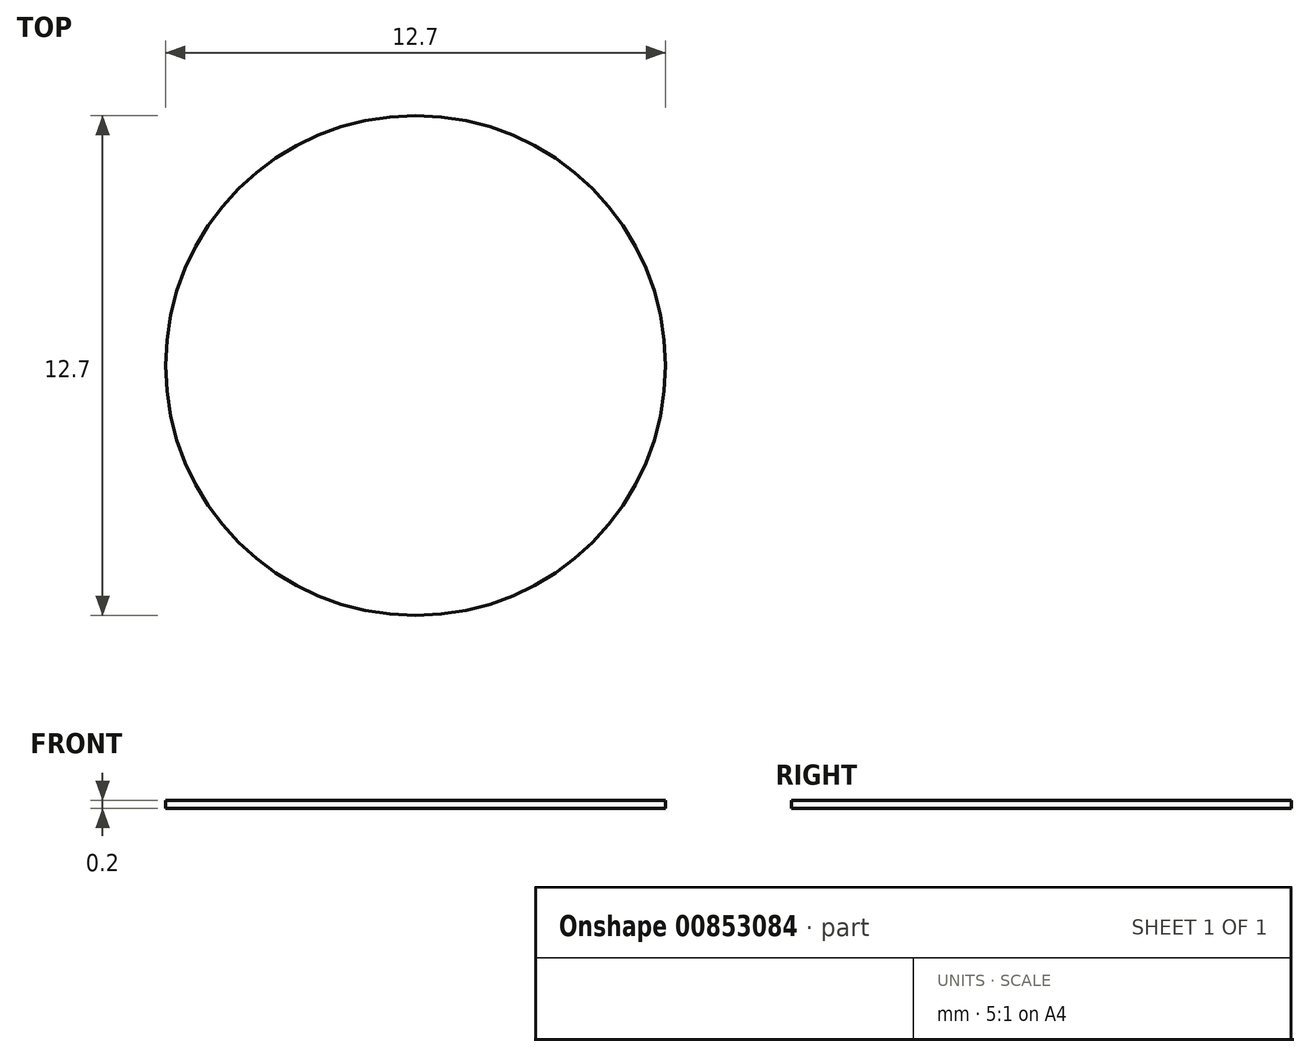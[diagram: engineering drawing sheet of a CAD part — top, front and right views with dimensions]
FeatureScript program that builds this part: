
annotation { "Feature Type Name" : "Feature", "Feature Type Description" : "" }
export const myFeature = defineFeature(function(context is Context, id is Id, definition is map)
    precondition{}
    {
        {
            var Q0;
            Q0=qCreatedBy(makeId("Top.planeOp"),FACE);
            var sketch = newSketch(context, id + "F0", { "sketchPlane" : qUnion([Q0])});
            skCircle(sketch, "E0", {"center": v(0, 0) * mm, "radius": 6.35 * mm});
            skSolve(sketch);
        }
        {
            var Q0;
            Q0 = qSketchRegion(id + "F0", true);
            extrude(context, id + "F1", {"entities" : qUnion([Q0]), "depth" : .2 * mm, "offsetDistance" : 25.4 * mm});
        }
    });
